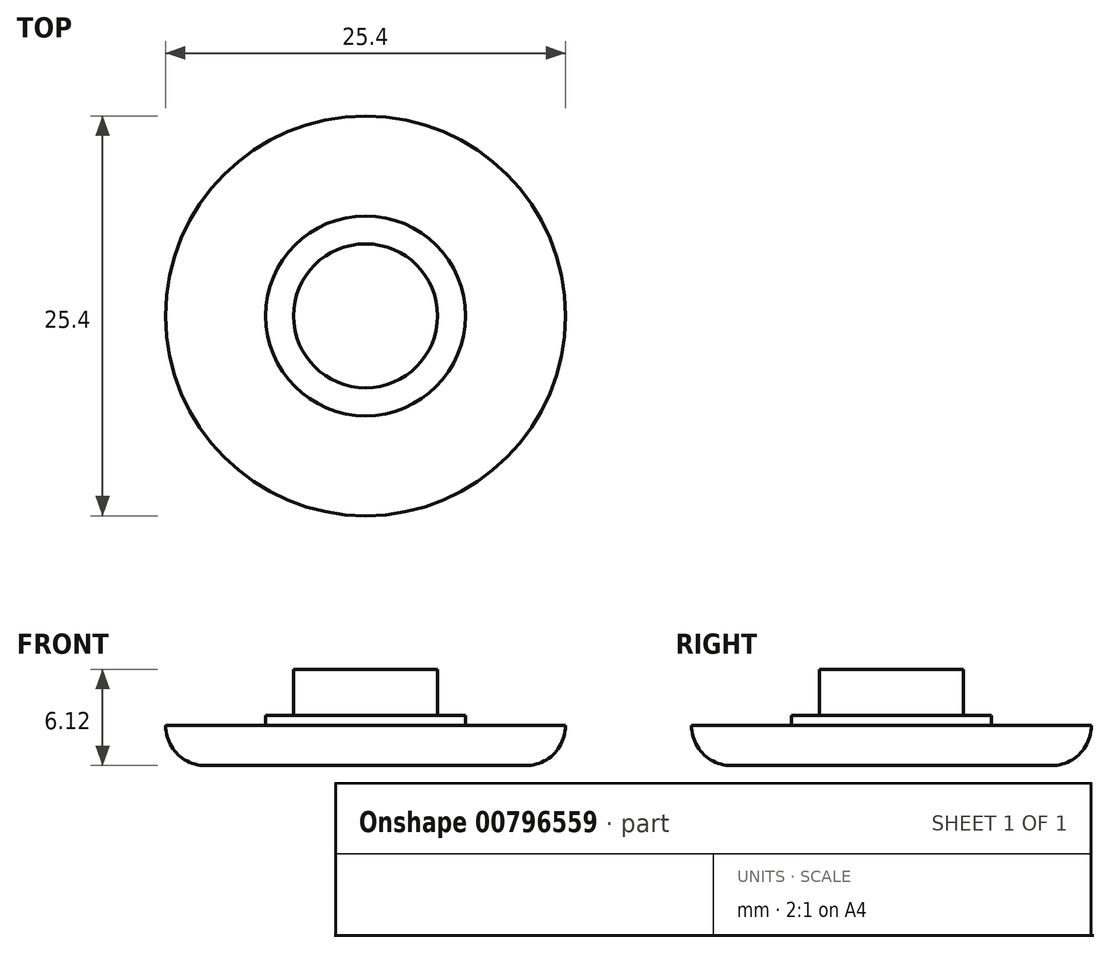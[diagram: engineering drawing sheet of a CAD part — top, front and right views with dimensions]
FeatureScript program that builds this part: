
annotation { "Feature Type Name" : "Feature", "Feature Type Description" : "" }
export const myFeature = defineFeature(function(context is Context, id is Id, definition is map)
    precondition{}
    {
        {
            var Q0;
            Q0=qCreatedBy(makeId("Top.planeOp"),FACE);
            var sketch = newSketch(context, id + "F0", { "sketchPlane" : qUnion([Q0])});
            skCircle(sketch, "E0", {"center": v(0, 0) * mm, "radius": 12.7 * mm});
            skSolve(sketch);
        }
        {
            var Q0;
            Q0=makeQuery(id+"F0.imprint","IMPRINT",FACE,{"disambiguationData":[TD([[makeQuery(id+"F0.imprint","IMPRINT",EDGE,{"derivedFrom":sQuery(id+"F0.wireOp",EDGE,"E0")}),1.0]])]});
            extrude(context, id + "F1", {"entities" : qUnion([Q0]), "depth" : 2.54 * mm, "offsetDistance" : 25.4 * mm});
        }
        {
            var Q0;
            Q0=makeQuery(id+"F1.opExtrude","CAP_EDGE",EDGE,{"disambiguationData":[OSD([sQuery(id+"F0.wireOp",EDGE,"E0")])],"isStart":true});
            fillet(context, id + "F2", {"entities" : qUnion([Q0]), "radius" : 2.54 * mm, "tangentPropagation" : true, "allowEdgeOverflow" : false});
        }
        {
            var Q0;
            Q0=makeQuery(id+"F1.opExtrude","CAP_FACE",FACE,{"disambiguationData":[OSD([sQuery(id+"F0.wireOp",EDGE,"E0")])],"isStart":false});
            var sketch = newSketch(context, id + "F3", { "sketchPlane" : qUnion([Q0])});
            skCircle(sketch, "E1", {"center": v(0, 0) * mm, "radius": 6.35 * mm});
            skSolve(sketch);
        }
        {
            var Q0;
            Q0=makeQuery(id+"F3.imprint","IMPRINT",FACE,{"disambiguationData":[TD([[makeQuery(id+"F3.imprint","IMPRINT",EDGE,{"derivedFrom":sQuery(id+"F3.wireOp",EDGE,"E1")}),1.0]])]});
            extrude(context, id + "F4", {"entities" : qUnion([Q0]), "operationType" : NewBodyOperationType.ADD, "depth" : 0.64 * mm, "offsetDistance" : 25.4 * mm});
        }
        {
            var Q0;
            Q0=makeQuery(id+"F4.opExtrude","CAP_FACE",FACE,{"disambiguationData":[OSD([sQuery(id+"F3.wireOp",EDGE,"E1")])],"isStart":false});
            var sketch = newSketch(context, id + "F5", { "sketchPlane" : qUnion([Q0])});
            skCircle(sketch, "E2", {"center": v(0, 0) * mm, "radius": 4.76 * mm});
            skSolve(sketch);
        }
        {
            var Q0;
            Q0=makeQuery(id+"F5.imprint","IMPRINT",FACE,{"disambiguationData":[TD([[makeQuery(id+"F5.imprint","IMPRINT",EDGE,{"derivedFrom":sQuery(id+"F5.wireOp",EDGE,"E2")}),1.0]])]});
            extrude(context, id + "F6", {"entities" : qUnion([Q0]), "operationType" : NewBodyOperationType.ADD, "depth" : 4.72 * mm, "offsetDistance" : 25.4 * mm});
        }
        {
            var Q0;
            Q0=makeQuery(id+"F6.opExtrude","CAP_FACE",FACE,{"disambiguationData":[OSD([sQuery(id+"F5.wireOp",EDGE,"E2")])],"isStart":false});
            var sketch = newSketch(context, id + "F7", { "sketchPlane" : qUnion([Q0])});
            skCircle(sketch, "E3", {"center": v(0, 0) * mm, "radius": 4.57 * mm});
            skCircle(sketch, "E4", {"center": v(0, 0) * mm, "radius": 4.76 * mm});
            skSolve(sketch);
        }
        {
            var Q0;
            Q0=makeQuery(id+"F7.imprint","IMPRINT",FACE,{"disambiguationData":[TD([[makeQuery(id+"F7.imprint","IMPRINT",EDGE,{"derivedFrom":sQuery(id+"F7.wireOp",EDGE,"E3")}),-1.0]])]});
            var Q1;
            Q1=makeQuery(id+"F4.opExtrude","CAP_FACE",FACE,{"disambiguationData":[OSD([sQuery(id+"F3.wireOp",EDGE,"E1")])],"isStart":false});
            extrude(context, id + "F8", {"entities" : qUnion([Q0]), "operationType" : NewBodyOperationType.REMOVE, "endBound" : BoundingType.UP_TO_SURFACE, "oppositeDirection" : true, "depth" : 25.4 * mm, "endBoundEntityFace" : qUnion([Q1]), "offsetDistance" : 25.4 * mm});
        }
        {
            var Q0;
            Q0=makeQuery(id+"F6.opExtrude","CAP_FACE",FACE,{"disambiguationData":[OSD([sQuery(id+"F5.wireOp",EDGE,"E2")])],"isStart":false});
            var sketch = newSketch(context, id + "F9", { "sketchPlane" : qUnion([Q0])});
            skCircle(sketch, "E5", {"center": v(0, 0) * mm, "radius": 4.57 * mm});
            skSolve(sketch);
        }
        {
            var Q0;
            Q0=makeQuery(id+"F9.imprint","IMPRINT",FACE,{"disambiguationData":[TD([[makeQuery(id+"F9.imprint","IMPRINT",EDGE,{"derivedFrom":sQuery(id+"F9.wireOp",EDGE,"E5")}),1.0]])]});
            extrude(context, id + "F10", {"entities" : qUnion([Q0]), "operationType" : NewBodyOperationType.REMOVE, "oppositeDirection" : true, "depth" : 1.78 * mm, "offsetDistance" : 25.4 * mm});
        }
    });
